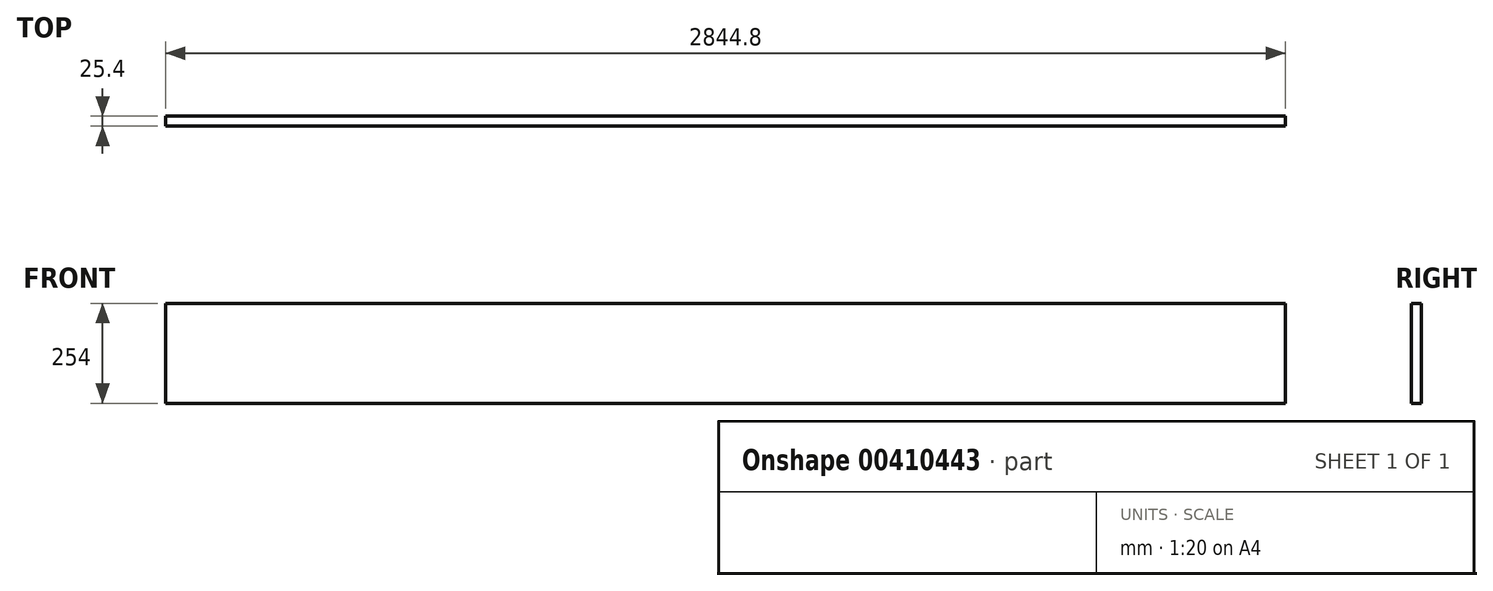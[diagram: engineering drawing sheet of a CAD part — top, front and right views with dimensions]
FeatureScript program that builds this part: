
annotation { "Feature Type Name" : "Feature", "Feature Type Description" : "" }
export const myFeature = defineFeature(function(context is Context, id is Id, definition is map)
    precondition{}
    {
        {
            var Q0;
            Q0=qCreatedBy(makeId("Front.planeOp"),FACE);
            var sketch = newSketch(context, id + "F0", { "sketchPlane" : qUnion([Q0])});
            skLineSegment(sketch, "E0.bottom", {"start": v(-1422.4, 127) * mm, "end": v(1422.4, 127) * mm});
            skLineSegment(sketch, "E0.top", {"start": v(-1422.4, -127) * mm, "end": v(1422.4, -127) * mm});
            skLineSegment(sketch, "E0.left", {"start": v(-1422.4, 127) * mm, "end": v(-1422.4, -127) * mm});
            skLineSegment(sketch, "E0.right", {"start": v(1422.4, 127) * mm, "end": v(1422.4, -127) * mm});
            skPoint(sketch, "E0.middle", {"position": v(0, 0) * mm});
            skSolve(sketch);
        }
        {
            var Q0;
            Q0=qSketchRegion(id+"F0",true);
            extrude(context, id + "F1", {"entities" : qUnion([Q0]), "depth" : 25.4 * mm, "offsetDistance" : 25.4 * mm});
        }
    });
